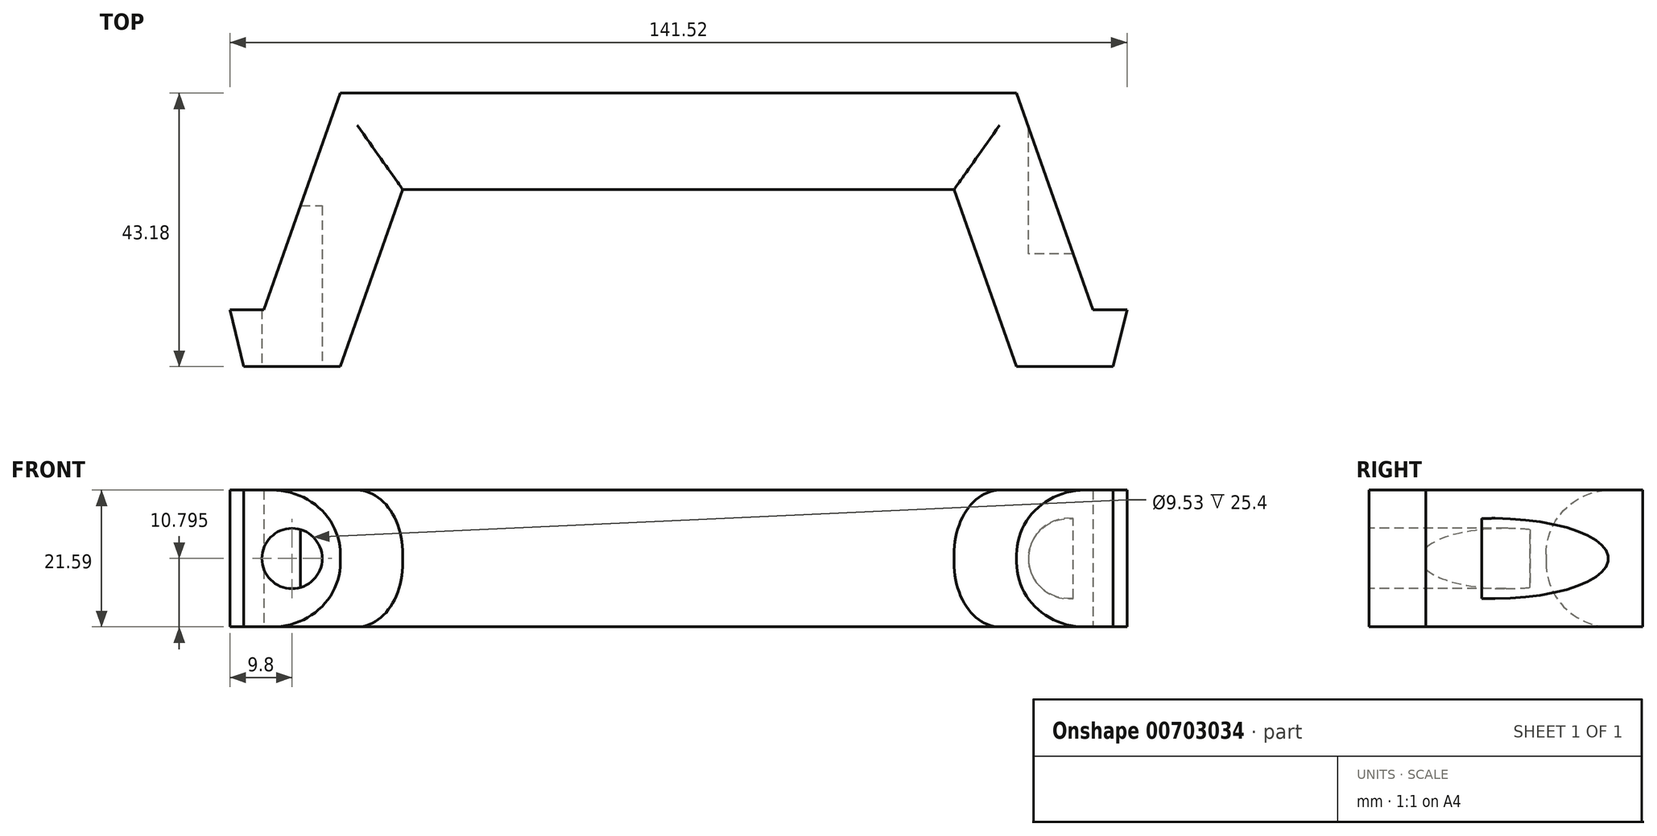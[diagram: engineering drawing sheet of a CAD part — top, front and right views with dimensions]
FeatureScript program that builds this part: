
annotation { "Feature Type Name" : "Feature", "Feature Type Description" : "" }
export const myFeature = defineFeature(function(context is Context, id is Id, definition is map)
    precondition{}
    {
        {
            var Q0;
            Q0=qCreatedBy(makeId("Top.planeOp"),FACE);
            var sketch = newSketch(context, id + "F0", { "sketchPlane" : qUnion([Q0])});
            skLineSegment(sketch, "E0", {"start": v(0, 0) * mm, "end": v(53.34, 0) * mm});
            skLineSegment(sketch, "E1", {"start": v(53.34, 0) * mm, "end": v(65.4, -34.2) * mm});
            skLineSegment(sketch, "E2", {"start": v(68.58, -43.18) * mm, "end": v(53.34, -43.18) * mm});
            skLineSegment(sketch, "E3", {"start": v(53.34, -43.18) * mm, "end": v(43.48, -15.24) * mm});
            skLineSegment(sketch, "E4", {"start": v(43.48, -15.24) * mm, "end": v(0, -15.24) * mm});
            skLineSegment(sketch, "E5", {"start": v(0, 36.63) * mm, "end": v(0, -40.2) * mm, "construction": true});
            skLineSegment(sketch, "E6.MirrorCS", {"start": v(0, 0) * mm, "end": v(-53.34, 0) * mm});
            skLineSegment(sketch, "E7.MirrorCS", {"start": v(-43.48, -15.24) * mm, "end": v(0, -15.24) * mm});
            skLineSegment(sketch, "E8.MirrorCS", {"start": v(-53.34, -43.18) * mm, "end": v(-43.48, -15.24) * mm});
            skLineSegment(sketch, "E9.MirrorCS", {"start": v(-68.58, -43.18) * mm, "end": v(-53.34, -43.18) * mm});
            skLineSegment(sketch, "E10.MirrorCS", {"start": v(-53.34, 0) * mm, "end": v(-65.4, -34.2) * mm});
            skLineSegment(sketch, "E11", {"start": v(-65.4, -34.2) * mm, "end": v(-70.76, -34.2) * mm});
            skLineSegment(sketch, "E12", {"start": v(-70.76, -34.2) * mm, "end": v(-68.58, -43.18) * mm});
            skPoint(sketch, "E13.orphan", {"position": v(-68.58, -43.18) * mm});
            skLineSegment(sketch, "E14.MirrorCS", {"start": v(70.76, -34.2) * mm, "end": v(68.58, -43.18) * mm});
            skLineSegment(sketch, "E15.MirrorCS", {"start": v(65.4, -34.2) * mm, "end": v(70.76, -34.2) * mm});
            skSolve(sketch);
        }
        {
            var Q0;
            Q0=makeQuery(id+"F0.imprint","IMPRINT",FACE,{"disambiguationData":[TD([[makeQuery(id+"F0.imprint","IMPRINT",EDGE,{"derivedFrom":sQuery(id+"F0.wireOp",EDGE,"E0")}),-1.0]])]});
            extrude(context, id + "F1", {"entities" : qUnion([Q0]), "depth" : 21.59 * mm, "offsetDistance" : 25.4 * mm});
        }
        {
            var Q0;
            Q0=makeQuery(id+"F1.opExtrude","SWEPT_FACE",FACE,{"disambiguationData":[OSD([sQuery(id+"F0.wireOp",EDGE,"E9.MirrorCS")])]});
            var sketch = newSketch(context, id + "F2", { "sketchPlane" : qUnion([Q0])});
            skCircle(sketch, "E16", {"center": v(-60.96, 10.8) * mm, "radius": 4.76 * mm});
            skLineSegment(sketch, "E17", {"start": v(-60.96, 21.59) * mm, "end": v(-60.96, 0) * mm, "construction": true});
            skLineSegment(sketch, "E18", {"start": v(-61.3, 1.1) * mm, "end": v(-68.58, 10.8) * mm, "construction": true});
            skLineSegment(sketch, "E19", {"start": v(-68.58, 10.8) * mm, "end": v(-56.2, 10.8) * mm, "construction": true});
            skCircle(sketch, "E20.MirrorC", {"center": v(60.96, 10.8) * mm, "radius": 4.76 * mm});
            skSolve(sketch);
        }
        {
            var Q0;
            Q0=makeQuery(id+"F2.imprint","IMPRINT",FACE,{"disambiguationData":[TD([[makeQuery(id+"F2.imprint","IMPRINT",EDGE,{"derivedFrom":sQuery(id+"F2.wireOp",EDGE,"E16")}),1.0]])]});
            var Q1;
            Q1=makeQuery(id+"F2.imprint","IMPRINT",FACE,{"disambiguationData":[TD([[makeQuery(id+"F2.imprint","IMPRINT",EDGE,{"derivedFrom":sQuery(id+"F2.wireOp",EDGE,"E20.MirrorC")}),-1.0]])]});
            extrude(context, id + "F3", {"entities" : qUnion([Q0, Q1]), "operationType" : NewBodyOperationType.REMOVE, "oppositeDirection" : true, "depth" : 25.4 * mm, "offsetDistance" : 25.4 * mm});
        }
        {
            var Q0;
            Q0=makeQuery(id+"F1.opExtrude","SWEPT_FACE",FACE,{"disambiguationData":[OSD([sQuery(id+"F0.wireOp",EDGE,"E0"),sQuery(id+"F0.wireOp",EDGE,"E6.MirrorCS")])]});
            var sketch = newSketch(context, id + "F4", { "sketchPlane" : qUnion([Q0])});
            skLineSegment(sketch, "E21", {"start": v(-61.57, 10.8) * mm, "end": v(9.54, 10.8) * mm});
            skPoint(sketch, "E21.startSnap0", {"position": v(-53.34, 10.8) * mm});
            skCircle(sketch, "E22", {"center": v(-61.57, 10.8) * mm, "radius": 6.35 * mm});
            skCircle(sketch, "E23.MirrorC", {"center": v(61.57, 10.8) * mm, "radius": 6.35 * mm});
            skSolve(sketch);
        }
        {
            var Q0;
            Q0=makeQuery(id+"F4.imprint","IMPRINT",FACE,{"disambiguationData":[TD([[makeQuery(id+"F4.imprint","IMPRINT",EDGE,{"derivedFrom":sQuery(id+"F4.wireOp",EDGE,"E22")}),1.0]])]});
            var Q1;
            Q1=makeQuery(id+"F4.imprint","IMPRINT",FACE,{"disambiguationData":[TD([[makeQuery(id+"F4.imprint","IMPRINT",EDGE,{"derivedFrom":sQuery(id+"F4.wireOp",EDGE,"E23.MirrorC")}),-1.0]])]});
            extrude(context, id + "F5", {"entities" : qUnion([Q0, Q1]), "operationType" : NewBodyOperationType.REMOVE, "oppositeDirection" : true, "depth" : 25.4 * mm, "offsetDistance" : 25.4 * mm});
        }
        {
            var Q0;
            Q0=makeQuery(id+"F1.opExtrude","CAP_EDGE",EDGE,{"disambiguationData":[OSD([sQuery(id+"F0.wireOp",EDGE,"E4"),sQuery(id+"F0.wireOp",EDGE,"E7.MirrorCS")])],"isStart":true});
            var Q1;
            Q1=makeQuery(id+"F1.opExtrude","CAP_EDGE",EDGE,{"disambiguationData":[OSD([sQuery(id+"F0.wireOp",EDGE,"E3")])],"isStart":true});
            var Q2;
            Q2=makeQuery(id+"F1.opExtrude","CAP_EDGE",EDGE,{"disambiguationData":[OSD([sQuery(id+"F0.wireOp",EDGE,"E8.MirrorCS")])],"isStart":true});
            var Q3;
            Q3=makeQuery(id+"F1.opExtrude","CAP_EDGE",EDGE,{"disambiguationData":[OSD([sQuery(id+"F0.wireOp",EDGE,"E3")])],"isStart":false});
            var Q4;
            Q4=makeQuery(id+"F1.opExtrude","CAP_EDGE",EDGE,{"disambiguationData":[OSD([sQuery(id+"F0.wireOp",EDGE,"E4"),sQuery(id+"F0.wireOp",EDGE,"E7.MirrorCS")])],"isStart":false});
            var Q5;
            Q5=makeQuery(id+"F1.opExtrude","CAP_EDGE",EDGE,{"disambiguationData":[OSD([sQuery(id+"F0.wireOp",EDGE,"E8.MirrorCS")])],"isStart":false});
            fillet(context, id + "F6", {"entities" : qUnion([Q0, Q1, Q2, Q3, Q4, Q5]), "radius" : 10.16 * mm, "tangentPropagation" : true, "allowEdgeOverflow" : false});
        }
    });
